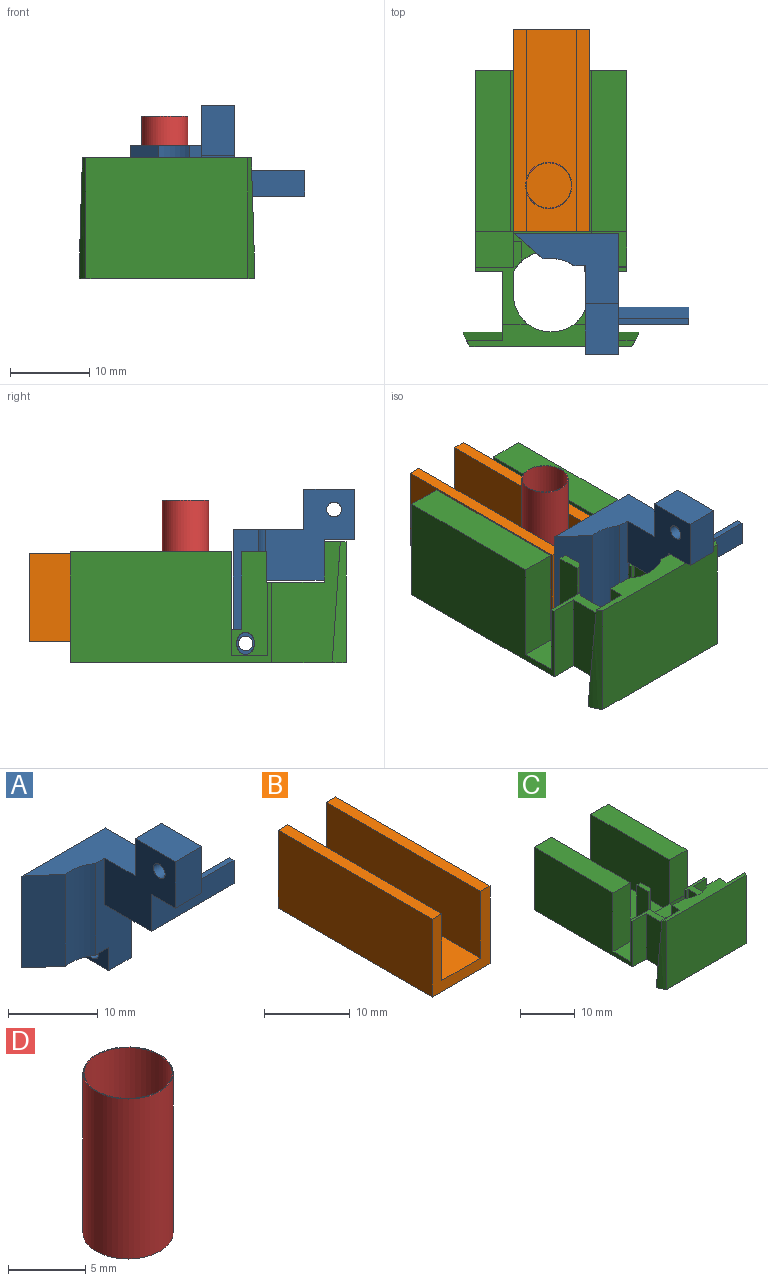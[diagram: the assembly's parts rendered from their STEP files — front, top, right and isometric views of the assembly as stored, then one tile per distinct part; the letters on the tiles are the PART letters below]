
ASSEMBLY  parts=4 mates=2
PART A: 21 faces, bbox 22.1x15.2x20.8 mm
  f0: plane 13.08x7.37mm, normal (0,0,-1), area 50.1mm2, adj f2,f3,f11,f12,f14,f15
  f1: plane 9.62x4.06mm, normal (0,0,-1), area 27.3mm2, adj f2,f4,f6,f7,f8
  f2: plane 15.72x5.61mm, normal (0,-1,0), area 55.2mm2, adj f0,f1,f3,f5,f6,f8,f9,f11
  f3: plane 20.8x15.24mm, normal (1,0,0), area 137.8mm2, adj f0,f2,f4,f5,f9,f10,f12,f13
  f4: plane 15.72x13.18mm, normal (0,1,0), area 176.9mm2, adj f1,f3,f5,f7,f8,f9
  f5: plane 13.18x8.89mm, normal (0,0,1), area 62mm2, adj f2,f3,f4,f6,f7,f11,f18
  f6: cylinder r=5.51mm len=12.57mm, axis (0,0,1), area 51.6mm2, adj f1,f2,f5,f7
  f7: plane 12.57x3.65mm, normal (-0.66,-0.76,0), area 60.8mm2, adj f1,f4,f5,f6
  f8: plane 4.06x3.15mm, normal (-1,0,0), area 10.2mm2, adj f1,f2,f4,f9,f10
  f9: plane 4.06x3.56mm, normal (0,0,-1), area 14.5mm2, adj f2,f3,f4,f8
  f10: cylinder r=0.91mm len=3.56mm, axis (1,0,0), area 20.4mm2, adj f3,f8
  f11: plane 11.43x11.18mm, normal (-1,0,0), area 81.2mm2, adj f0,f2,f5,f12,f16,f17,f18,f19
  f12: plane 13.08x5.08mm, normal (0,-1,0), area 49.5mm2, adj f0,f3,f11,f13,f14,f16
  f13: plane 8.89x0.76mm, normal (0,0,1), area 6.8mm2, adj f3,f12,f14,f15
  f14: plane 3.18x2.16mm, normal (1,0,0), area 4.6mm2, adj f0,f12,f13,f15
  f15: plane 8.89x3.18mm, normal (0,0.92,0.4), area 30.8mm2, adj f0,f3,f13,f14
  f16: plane 4.19x3.81mm, normal (0,0,-1), area 16mm2, adj f3,f11,f12,f17
  f17: plane 6.35x4.19mm, normal (0,-1,0), area 26.6mm2, adj f3,f11,f16,f19
  f18: plane 5.08x4.19mm, normal (0,1,0), area 21.3mm2, adj f3,f5,f11,f19
  f19: plane 6.35x4.19mm, normal (0,0,1), area 26.6mm2, adj f3,f11,f17,f18
  f20: cylinder r=0.93mm len=4.19mm, axis (1,0,0), area 24.4mm2, adj f3,f11
PART B: 10 faces, bbox 9.5x25.4x11.1 mm
  f0: plane 25.4x6.35mm, normal (0,0,1), area 161.3mm2, adj f4,f5,f6,f8
  f1: plane 25.4x11.11mm, normal (-1,0,0), area 282.3mm2, adj f2,f4,f5,f7
  f2: plane 25.4x9.53mm, normal (0,0,-1), area 241.9mm2, adj f1,f3,f4,f5
  f3: plane 25.4x11.11mm, normal (1,0,0), area 282.3mm2, adj f2,f4,f5,f9
  f4: plane 11.11x9.53mm, normal (0,-1,0), area 45.4mm2, adj f0,f1,f2,f3,f6,f7,f8,f9
  f5: plane 11.11x9.53mm, normal (0,1,0), area 45.4mm2, adj f0,f1,f2,f3,f6,f7,f8,f9
  f6: plane 25.4x9.53mm, normal (1,0,0), area 241.9mm2, adj f0,f4,f5,f7
  f7: plane 25.4x1.59mm, normal (0,0,1), area 40.3mm2, adj f1,f4,f5,f6
  f8: plane 25.4x9.53mm, normal (-1,0,0), area 241.9mm2, adj f0,f4,f5,f9
  f9: plane 25.4x1.59mm, normal (0,0,1), area 40.3mm2, adj f3,f4,f5,f8
PART C: 50 faces, bbox 22.4x35x15.4 mm
  f0: plane 25.4x13.97mm, normal (1,0,0), area 293.9mm2, adj f6,f11,f12,f16,f17,f23,f28,f36
  f1: plane 25.4x13.97mm, normal (-1,0,0), area 293.1mm2, adj f6,f17,f21,f22,f31,f32,f33,f44
  f2: cylinder r=12.29mm len=15.24mm, axis (0,0,1), area 21.9mm2, adj f3,f4,f5,f6
  f3: plane 20.42x15.24mm, normal (0,-1,0), area 311.2mm2, adj f2,f4,f6,f49
  f4: plane 21.29x2.79mm, normal (0,0,1), area 36.7mm2, adj f2,f3,f5,f7,f18,f19,f30,f45
  f5: plane 15.4x5.17mm, normal (0,1,0.07), area 73mm2, adj f2,f4,f6,f19
  f6: plane 34.82x22.19mm, normal (0,0,-1), area 533.4mm2, adj f0,f1,f2,f3,f5,f7,f14,f15
  f7: plane 15.44x5.22mm, normal (0,1,0.07), area 73.6mm2, adj f4,f6,f18,f20,f49
  f8: plane 5.97x0.52mm, normal (0,-1,0), area 3.1mm2, adj f9,f15,f40,f47
  f9: plane 0.52x0.51mm, normal (0,0,-1), area 0.2mm2, adj f8,f11,f29,f40
  f10: plane 9.78x2.47mm, normal (1,0,0), area 24.1mm2, adj f12,f13,f41,f42
  f11: plane 5.97x5.28mm, normal (0,1,0), area 31.5mm2, adj f0,f9,f12,f40,f47
  f12: plane 14.22x4.57mm, normal (0,0,1), area 28.7mm2, adj f0,f10,f11,f25,f28,f29,f34,f36
  f13: plane 3.12x1.02mm, normal (0,0,1), area 2.9mm2, adj f10,f34,f41,f42,f48
  f14: plane 10.16x3.07mm, normal (1,0,0), area 31.1mm2, adj f6,f29,f30,f42,f44
  f15: plane 10.16x3.07mm, normal (-1,0,0), area 31.1mm2, adj f6,f8,f29,f30,f47
  f16: plane 20.32x4.45mm, normal (0,0,1), area 90.3mm2, adj f0,f17,f26,f28
  f17: plane 19.05x13.97mm, normal (0,1,0), area 150mm2, adj f0,f1,f6,f16,f22,f24,f26,f27
  f18: plane 15.24x8.65mm, normal (-1,0,0), area 90.5mm2, adj f4,f6,f7,f21,f44,f45
  f19: plane 15.24x8.65mm, normal (1,0,0), area 90.5mm2, adj f4,f5,f6,f23,f46,f47
  f20: plane 0.5x0.03mm, normal (-1,0,0), area 0mm2, adj f6,f7,f49
  f21: plane 10.16x3.44mm, normal (0,-1,0), area 35mm2, adj f1,f6,f18,f44
  f22: plane 20.32x4.45mm, normal (0,0,1), area 90.3mm2, adj f1,f17,f24,f31
  f23: plane 10.16x3.44mm, normal (0,-1,0), area 35mm2, adj f0,f6,f19,f47
  f24: plane 20.32x11.43mm, normal (1,0,0), area 232.3mm2, adj f17,f22,f27,f31
  f25: plane 9.78x1.65mm, normal (0,1,0), area 16.1mm2, adj f12,f26,f27,f34
  f26: plane 20.32x11.43mm, normal (-1,0,0), area 232.3mm2, adj f16,f17,f25,f27,f28
  f27: plane 20.32x10.16mm, normal (0,0,1), area 206.5mm2, adj f17,f24,f25,f26,f31
  f28: plane 9.78x4.45mm, normal (0,-1,0), area 43.5mm2, adj f0,f12,f16,f26
  f29: cylinder r=5.49mm len=9.53mm, axis (0,0,1), area 37.8mm2, adj f6,f9,f12,f14,f15,f35,f43
  f30: cylinder r=4.77mm len=15.24mm, axis (0,0,1), area 179.2mm2, adj f4,f6,f14,f15,f44,f45,f46,f47
  f31: plane 13.08x4.83mm, normal (0,-1,0), area 58.8mm2, adj f1,f22,f24,f27,f32,f34
  f32: plane 4.83x4.57mm, normal (0,0,1), area 22.1mm2, adj f1,f31,f33,f34
  f33: plane 9.27x4.83mm, normal (0,1,0), area 44.7mm2, adj f1,f32,f34,f44
  f34: plane 13.08x4.57mm, normal (-1,0,0), area 41.7mm2, adj f12,f13,f25,f31,f32,f33,f35,f41
  f35: extruded ~9.78x2.79mm, area 67mm2, adj f29,f34,f39
  f36: plane 4.45x3.3mm, normal (0,1,0), area 14.7mm2, adj f0,f12,f37,f39
  f37: plane 4.45x4.34mm, normal (0,0,1), area 19.3mm2, adj f0,f36,f38,f39
  f38: plane 4.45x3.3mm, normal (0,-1,0), area 14.7mm2, adj f0,f12,f37,f39
  f39: plane 4.34x3.3mm, normal (1,0,0), area 9.3mm2, adj f12,f35,f36,f37,f38
  f40: plane 5.97x0.51mm, normal (-1,0,0), area 3mm2, adj f8,f9,f11,f47
  f41: plane 9.78x1.02mm, normal (0,1,0), area 9.9mm2, adj f10,f12,f13,f34
  f42: cylinder r=3.65mm len=9.78mm, axis (0,0,1), area 13.9mm2, adj f10,f13,f14,f43,f44,f48
  f43: plane 1.34x1.08mm, normal (0,0,1), area 0mm2, adj f29,f42
  f44: plane 7.31x6.63mm, normal (0,0,1), area 13.4mm2, adj f1,f14,f18,f21,f30,f33,f34,f42
  f45: plane 5.08x3.18mm, normal (0,1,0), area 16.2mm2, adj f4,f18,f30,f44
  f46: plane 5.08x3.18mm, normal (0,1,0), area 16.2mm2, adj f4,f19,f30,f47
  f47: plane 7.13x6.63mm, normal (0,0,1), area 13.5mm2, adj f0,f8,f11,f15,f19,f23,f30,f40
  f48: plane 3.81x0.36mm, normal (0,-1,0), area 1.4mm2, adj f13,f34,f42,f44
  f49: cylinder r=8.41mm len=15.24mm, axis (0,0,1), area 21.9mm2, adj f3,f4,f6,f7,f20
PART D: 4 faces, bbox 5.8x5.8x12.7 mm
  f0: cylinder r=2.86mm len=12.7mm, axis (0,0,-1), area 228mm2, adj f2,f3
  f1: cylinder r=2.92mm len=12.7mm, axis (0,0,-1), area 233.1mm2, adj f2,f3
  f2: plane 5.84x5.84mm, normal (0,0,1), area 1.2mm2, adj f0,f1
  f3: plane 5.84x5.84mm, normal (0,0,-1), area 1.2mm2, adj f0,f1
PLACE A t=(-10.76,11.04,14.79)mm
PLACE B rot(axis=(0,-1,0),0deg) t=(-14.45,44.63,26.33)mm fixed
PLACE C t=(-9.74,11.04,14.79)mm fixed
PLACE D t=(-10.02,24.98,31.49)mm
MATE parallel C.f17 <-> B.f4  axis (0,1,0) through (-0.21,39.5,30.66)mm
MATE slider A.f10 <-> C.f39  axis (1,0,0) through (-1.23,17.41,26.09)mm
